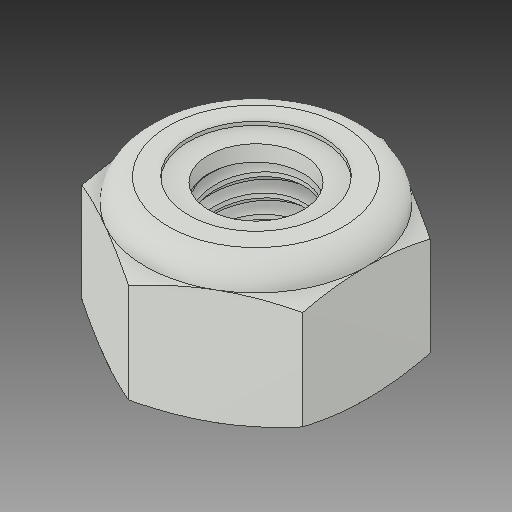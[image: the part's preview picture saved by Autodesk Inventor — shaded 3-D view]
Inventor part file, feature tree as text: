
AUTODESK INVENTOR PART (.ipt)
format: ipt  version: 2018 (Build 220112000, 112)  size: 307,200 bytes
history: native  units: in
note: dims shown in document units (in); Inventor stores cm internally (conversion verified against a paired STEP export)
features: other x1, revolve x1
ambient origin geometry x8: Origin, YZ Plane, XZ Plane, XY Plane, X Axis, Y Axis, Z Axis, Center Point
bodies: Solid1 (feature_tree), Solid2 (feature_tree)
feature tree (2):
  other  "Cut-Revolve4"
  revolve  "Revolve2"  [1 undecoded]
note: 1 required parameter value undecoded (feature->parameter linkage not recoverable at this tier; creation-order binding heuristic only, values carry confidence <= 0.55)
